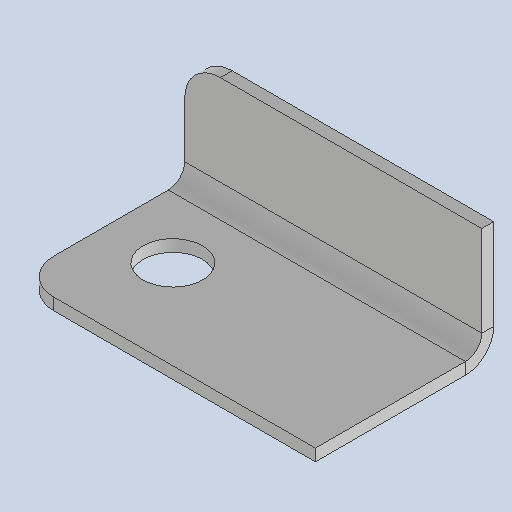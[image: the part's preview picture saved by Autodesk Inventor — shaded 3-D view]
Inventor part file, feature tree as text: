
AUTODESK INVENTOR PART (.ipt)
format: ipt  version: 2025 (Build 290162010, 162A)  size: 162,304 bytes
history: native  units: mm
features: sheet_metal_op x4, other x4, sketch x3, chamfer x1
ambient origin geometry x8: Origin, YZ Plane, XZ Plane, XY Plane, X Axis, Y Axis, Z Axis, Center Point
bodies: Body1 (feature_tree)
feature tree (12):
  sheet_metal_op  "Face1"
  sheet_metal_op  "Flange1"
  chamfer  "Corner Round1"
  sketch  "Sketch2"  dims[d7=2.0mm]
  other  "Plate1"
  sketch  "Sketch3"  dims[d10=30.0mm]
  other  "Plate2"
  sheet_metal_op  "Bend1"
  sheet_metal_op  "Corner1"
  sketch  "Sketch4"  dims[d14=2.0mm d15=1.0mm d16=4.0mm d17=2.75mm d18=20.0mm d19=90.0deg d20=2.75mm d21=8.0mm d22=2.0mm d23=2.75mm d24=6.0mm d25=10.0mm d26=15.0mm d27=5.0mm d28=2.0mm d29=0.0mm d30=50.0mm]
  other  "Cut1"
  other  "Definition1"
